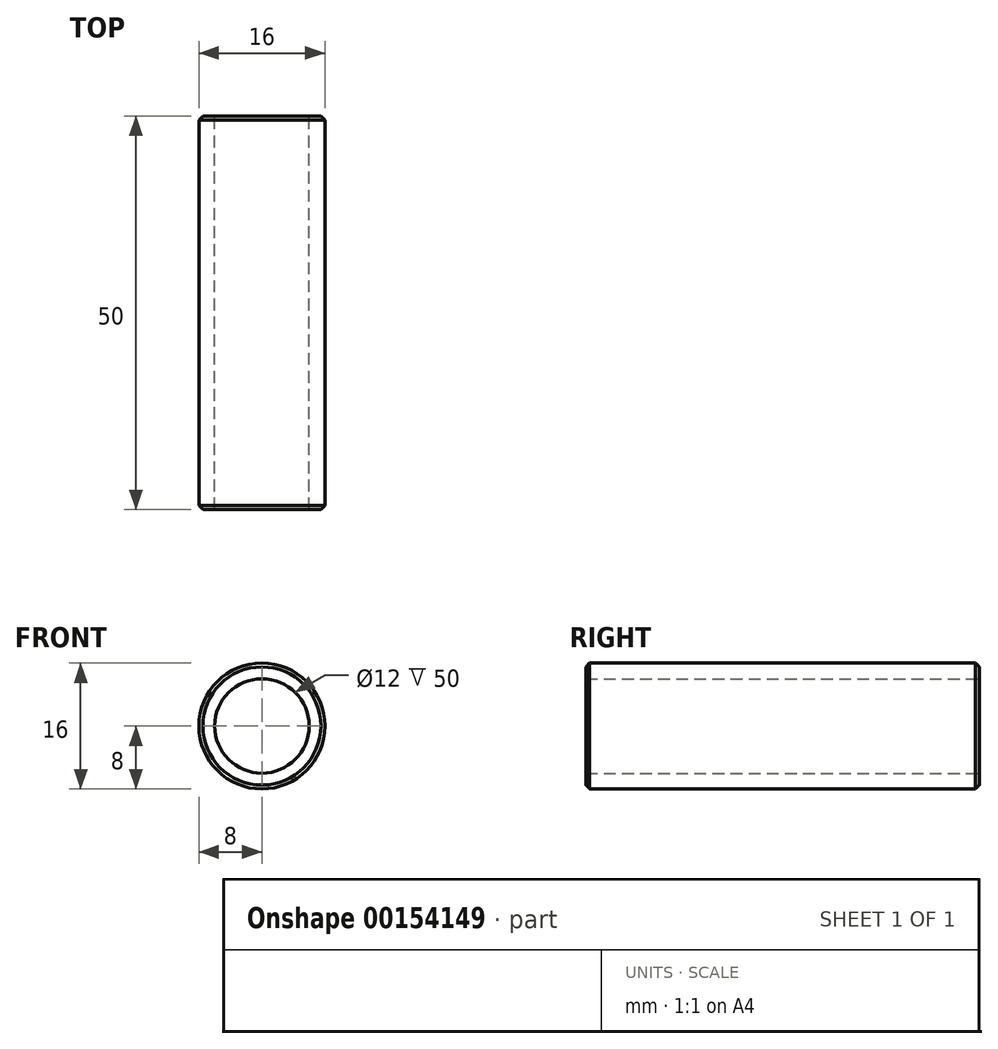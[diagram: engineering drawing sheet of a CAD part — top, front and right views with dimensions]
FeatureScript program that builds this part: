
annotation { "Feature Type Name" : "Feature", "Feature Type Description" : "" }
export const myFeature = defineFeature(function(context is Context, id is Id, definition is map)
    precondition{}
    {
        {
            var Q0;
            Q0=qCreatedBy(makeId("Front.planeOp"),FACE);
            var sketch = newSketch(context, id + "F0", { "sketchPlane" : qUnion([Q0])});
            skCircle(sketch, "E0", {"center": v(0, 0) * mm, "radius": 8 * mm});
            skCircle(sketch, "E1", {"center": v(0, 0) * mm, "radius": 6 * mm});
            skSolve(sketch);
        }
        {
            var Q0;
            Q0 = qSketchRegion(id + "F0", true);
            extrude(context, id + "F1", {"entities" : qUnion([Q0]), "depth" : 50 * mm});
        }
        {
            var Q0;
            Q0=makeQuery(id+"F1.opExtrude","CAP_EDGE",EDGE,{"disambiguationData":[OSD([sQuery(id+"F0.wireOp",EDGE,"E0")])],"isStart":false});
            var Q1;
            Q1=makeQuery(id+"F1.opExtrude","CAP_EDGE",EDGE,{"disambiguationData":[OSD([sQuery(id+"F0.wireOp",EDGE,"E0")])],"isStart":true});
            chamfer(context, id + "F2", {"entities" : qUnion([Q0, Q1]), "width" : .5 * mm, "tangentPropagation" : true});
        }
    });
